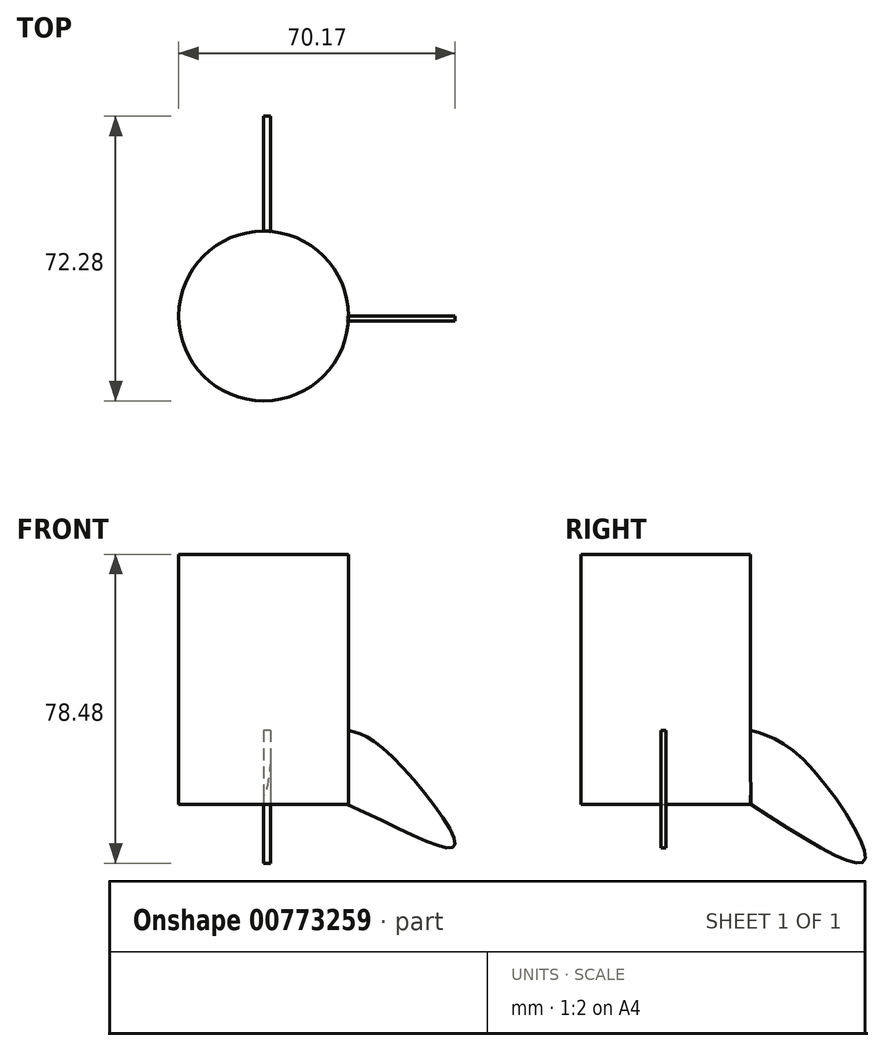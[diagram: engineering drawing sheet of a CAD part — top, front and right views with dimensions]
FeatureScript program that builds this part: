
annotation { "Feature Type Name" : "Feature", "Feature Type Description" : "" }
export const myFeature = defineFeature(function(context is Context, id is Id, definition is map)
    precondition{}
    {
        {
            var Q0;
            Q0=qCreatedBy(makeId("Top.planeOp"),FACE);
            var sketch = newSketch(context, id + "F0", { "sketchPlane" : qUnion([Q0])});
            skCircle(sketch, "E0", {"center": v(0, 0) * mm, "radius": 21.56 * mm});
            skSolve(sketch);
        }
        {
            var Q0;
            Q0 = qSketchRegion(id + "F0", true);
            extrude(context, id + "F1", {"entities" : qUnion([Q0]), "depth" : 63.5 * mm, "offsetDistance" : 25.4 * mm});
        }
        {
            var Q0;
            Q0=qCreatedBy(makeId("Right.planeOp"),FACE);
            var sketch = newSketch(context, id + "F2", { "sketchPlane" : qUnion([Q0])});
            skFitSpline(sketch, "E1", {"points": [v(21.42, 18.83) * mm, v(34.66, 11.58) * mm, v(50.58, -14.17) * mm, v(21.58, 0) * mm], "startDerivative": vector(46.46, -12.7) * mm, "endDerivative": vector(-109.28, 70.59) * mm});
            skLineSegment(sketch, "E2", {"start": v(21.42, 18.83) * mm, "end": v(21.58, 0) * mm});
            skSolve(sketch);
        }
        {
            var Q0;
            Q0 = qSketchRegion(id + "F2", true);
            extrude(context, id + "F3", {"entities" : qUnion([Q0]), "operationType" : NewBodyOperationType.ADD, "depth" : 1.78 * mm, "offsetDistance" : 25.4 * mm});
        }
        {
            var Q0;
            Q0=qCreatedBy(makeId("Front.planeOp"),FACE);
            var sketch = newSketch(context, id + "F4", { "sketchPlane" : qUnion([Q0])});
            skLineSegment(sketch, "E3", {"start": v(21.22, 0) * mm, "end": v(21.22, 18.82) * mm});
            skFitSpline(sketch, "E4", {"points": [v(21.22, 18.82) * mm, v(30.37, 14.2) * mm, v(48.56, -10.34) * mm, v(21.22, 0) * mm], "startDerivative": vector(34.87, -7.36) * mm, "endDerivative": vector(-103.66, 45.92) * mm});
            skSolve(sketch);
        }
        {
            var Q0;
            Q0 = qSketchRegion(id + "F4", true);
            extrude(context, id + "F5", {"entities" : qUnion([Q0]), "operationType" : NewBodyOperationType.ADD, "depth" : 1.27 * mm, "offsetDistance" : 25.4 * mm});
        }
    });
